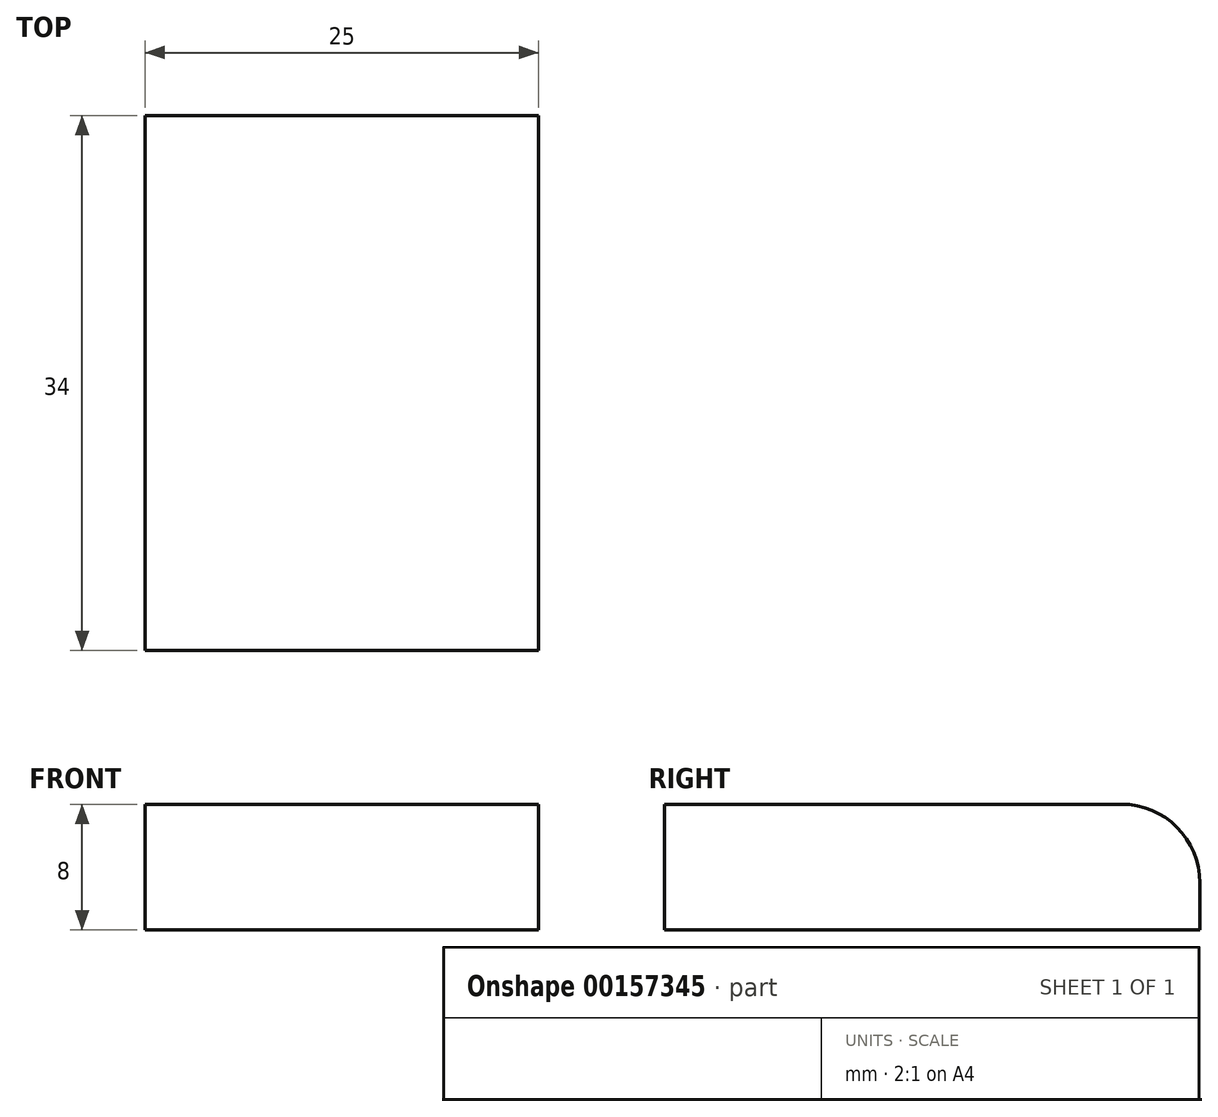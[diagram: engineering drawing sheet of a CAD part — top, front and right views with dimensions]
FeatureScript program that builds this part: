
annotation { "Feature Type Name" : "Feature", "Feature Type Description" : "" }
export const myFeature = defineFeature(function(context is Context, id is Id, definition is map)
    precondition{}
    {
        {
            var Q0;
            Q0=qCreatedBy(makeId("Top.planeOp"),FACE);
            var sketch = newSketch(context, id + "F0", { "sketchPlane" : qUnion([Q0])});
            skLineSegment(sketch, "E0.bottom", {"start": v(12.5, 17) * mm, "end": v(-12.5, 17) * mm});
            skLineSegment(sketch, "E0.top", {"start": v(12.5, -17) * mm, "end": v(-12.5, -17) * mm});
            skLineSegment(sketch, "E0.left", {"start": v(12.5, 17) * mm, "end": v(12.5, -17) * mm});
            skLineSegment(sketch, "E0.right", {"start": v(-12.5, 17) * mm, "end": v(-12.5, -17) * mm});
            skPoint(sketch, "E0.middle", {"position": v(0, 0) * mm});
            skSolve(sketch);
        }
        {
            var Q0;
            Q0=makeQuery(id+"F0.imprint","IMPRINT",FACE,{"disambiguationData":[TD([[makeQuery(id+"F0.imprint","IMPRINT",EDGE,{"derivedFrom":sQuery(id+"F0.wireOp",EDGE,"E0.bottom")}),1.0]])]});
            extrude(context, id + "F1", {"entities" : qUnion([Q0]), "depth" : 8 * mm});
        }
        {
            var Q0;
            Q0=makeQuery(id+"F1.opExtrude","CAP_EDGE",EDGE,{"disambiguationData":[OSD([sQuery(id+"F0.wireOp",EDGE,"E0.bottom")])],"isStart":false});
            fillet(context, id + "F2", {"entities" : qUnion([Q0]), "radius" : 5 * mm, "tangentPropagation" : true, "allowEdgeOverflow" : false});
        }
    });
